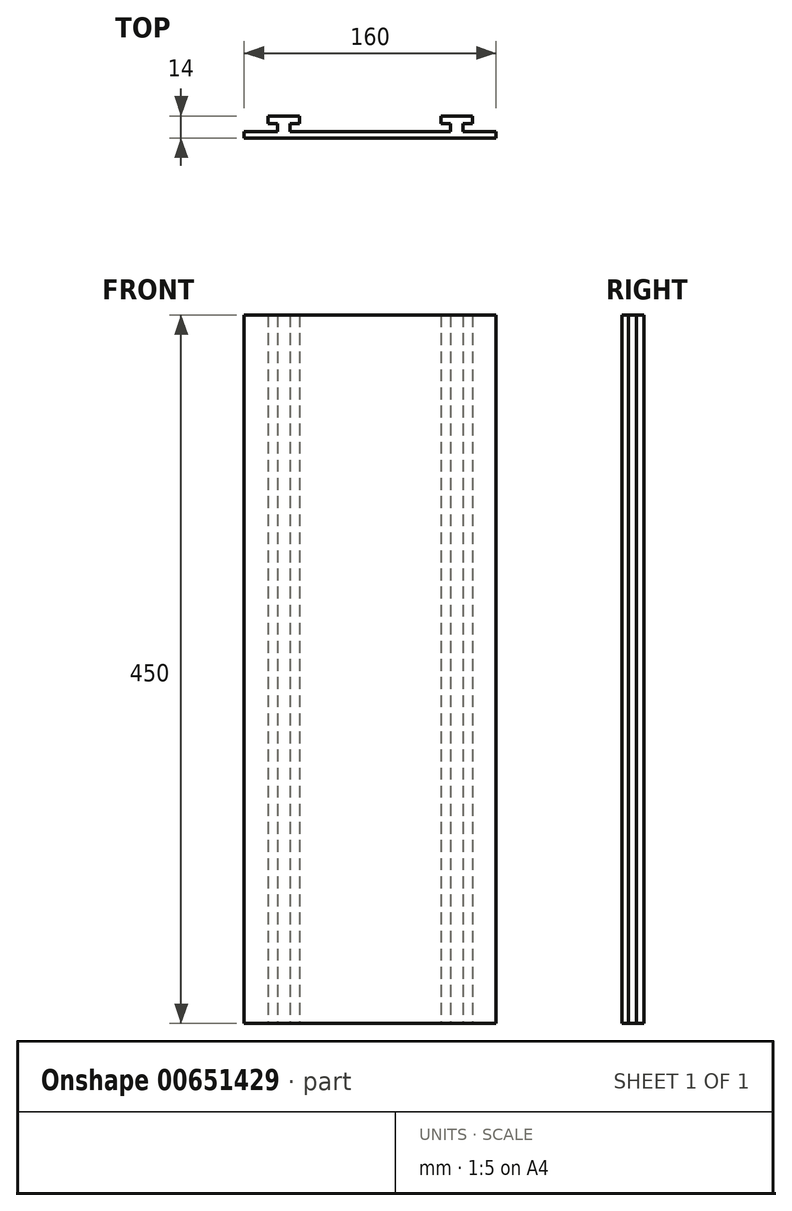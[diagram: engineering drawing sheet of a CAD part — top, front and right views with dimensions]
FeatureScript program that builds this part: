
annotation { "Feature Type Name" : "Feature", "Feature Type Description" : "" }
export const myFeature = defineFeature(function(context is Context, id is Id, definition is map)
    precondition{}
    {
        {
            var Q0;
            Q0=qCreatedBy(makeId("Top.planeOp"),FACE);
            var sketch = newSketch(context, id + "F0", { "sketchPlane" : qUnion([Q0])});
            skLineSegment(sketch, "E0", {"start": v(80, 0) * mm, "end": v(80, 4) * mm});
            skLineSegment(sketch, "E1", {"start": v(80, 4) * mm, "end": v(59, 4) * mm});
            skLineSegment(sketch, "E2", {"start": v(59, 4) * mm, "end": v(59, 9) * mm});
            skLineSegment(sketch, "E3", {"start": v(59, 9) * mm, "end": v(65, 9) * mm});
            skLineSegment(sketch, "E4", {"start": v(65, 9) * mm, "end": v(65, 14) * mm});
            skLineSegment(sketch, "E5", {"start": v(65, 14) * mm, "end": v(45, 14) * mm});
            skLineSegment(sketch, "E6", {"start": v(45, 14) * mm, "end": v(45, 9) * mm});
            skLineSegment(sketch, "E7", {"start": v(45, 9) * mm, "end": v(51, 9) * mm});
            skLineSegment(sketch, "E8", {"start": v(51, 9) * mm, "end": v(51, 4) * mm});
            skLineSegment(sketch, "E9", {"start": v(0, 0) * mm, "end": v(80, 0) * mm});
            skLineSegment(sketch, "E10.MirrorCS", {"start": v(-65, 14) * mm, "end": v(-45, 14) * mm});
            skLineSegment(sketch, "E11.MirrorCS", {"start": v(-45, 14) * mm, "end": v(-45, 9) * mm});
            skLineSegment(sketch, "E12.MirrorCS", {"start": v(-45, 9) * mm, "end": v(-51, 9) * mm});
            skLineSegment(sketch, "E13.MirrorCS", {"start": v(-51, 9) * mm, "end": v(-51, 4) * mm});
            skLineSegment(sketch, "E14.MirrorCS", {"start": v(-65, 9) * mm, "end": v(-65, 14) * mm});
            skLineSegment(sketch, "E15.MirrorCS", {"start": v(-59, 9) * mm, "end": v(-65, 9) * mm});
            skLineSegment(sketch, "E16.MirrorCS", {"start": v(-59, 4) * mm, "end": v(-59, 9) * mm});
            skLineSegment(sketch, "E17.MirrorCS", {"start": v(-80, 4) * mm, "end": v(-59, 4) * mm});
            skLineSegment(sketch, "E18.MirrorCS", {"start": v(-80, 0) * mm, "end": v(-80, 4) * mm});
            skLineSegment(sketch, "E19.MirrorCS", {"start": v(0, 0) * mm, "end": v(-80, 0) * mm});
            skLineSegment(sketch, "E20", {"start": v(-51, 4) * mm, "end": v(51, 4) * mm});
            skSolve(sketch);
        }
        {
            var Q0;
            Q0 = qSketchRegion(id + "F0", true);
            extrude(context, id + "F1", {"entities" : qUnion([Q0]), "depth" : 450 * mm, "offsetDistance" : 25 * mm});
        }
    });
